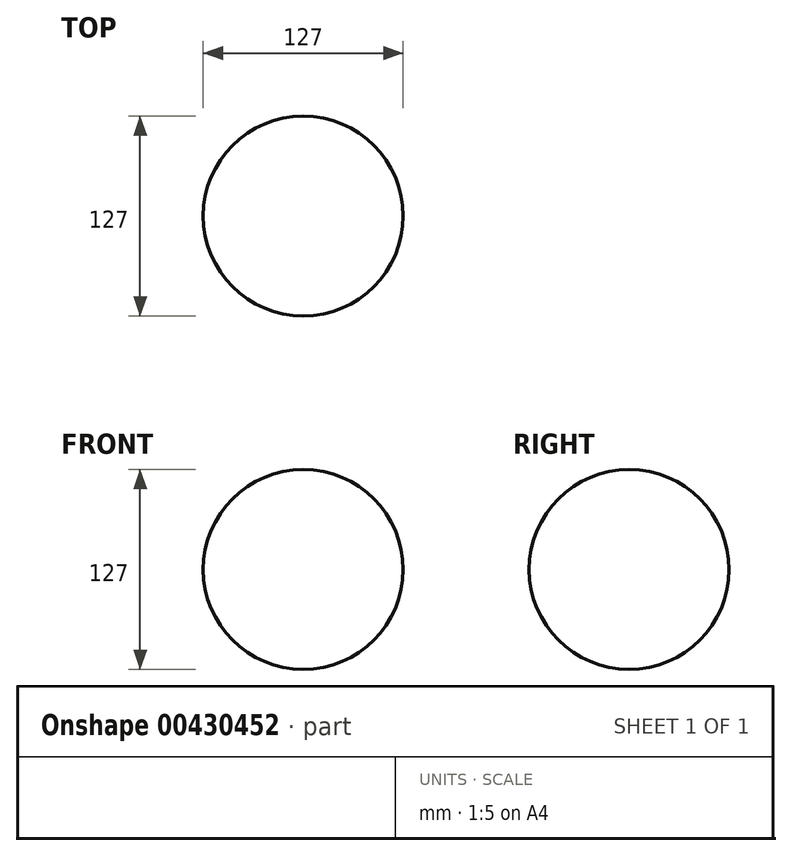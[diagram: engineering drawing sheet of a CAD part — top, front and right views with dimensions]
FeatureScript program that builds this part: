
annotation { "Feature Type Name" : "Feature", "Feature Type Description" : "" }
export const myFeature = defineFeature(function(context is Context, id is Id, definition is map)
    precondition{}
    {
        {
            var Q0;
            Q0=qCreatedBy(makeId("Front.planeOp"),FACE);
            var sketch = newSketch(context, id + "F0", { "sketchPlane" : qUnion([Q0])});
            skCircle(sketch, "E0", {"center": v(0, 0) * mm, "radius": 63.5 * mm});
            skLineSegment(sketch, "E1", {"start": v(0, 63.5) * mm, "end": v(0, -63.5) * mm});
            skSolve(sketch);
        }
        {
            var Q0;
            {var subQ0=sQuery(id+"F0.wireOp",EDGE,"E1");Q0=makeQuery(id+"F0.imprint","IMPRINT",FACE,{"disambiguationData":[TD([[makeQuery(id+"F0.imprint","IMPRINT",EDGE,{"derivedFrom":subQ0}),-1.0]])]});}
            var Q1;
            Q1=sQuery(id+"F0.wireOp",EDGE,"E1");
            revolve(context, id + "F1", {"entities" : qUnion([Q0]), "axis" : qUnion([Q1]), "revolveType" : RevolveType.FULL});
        }
    });
